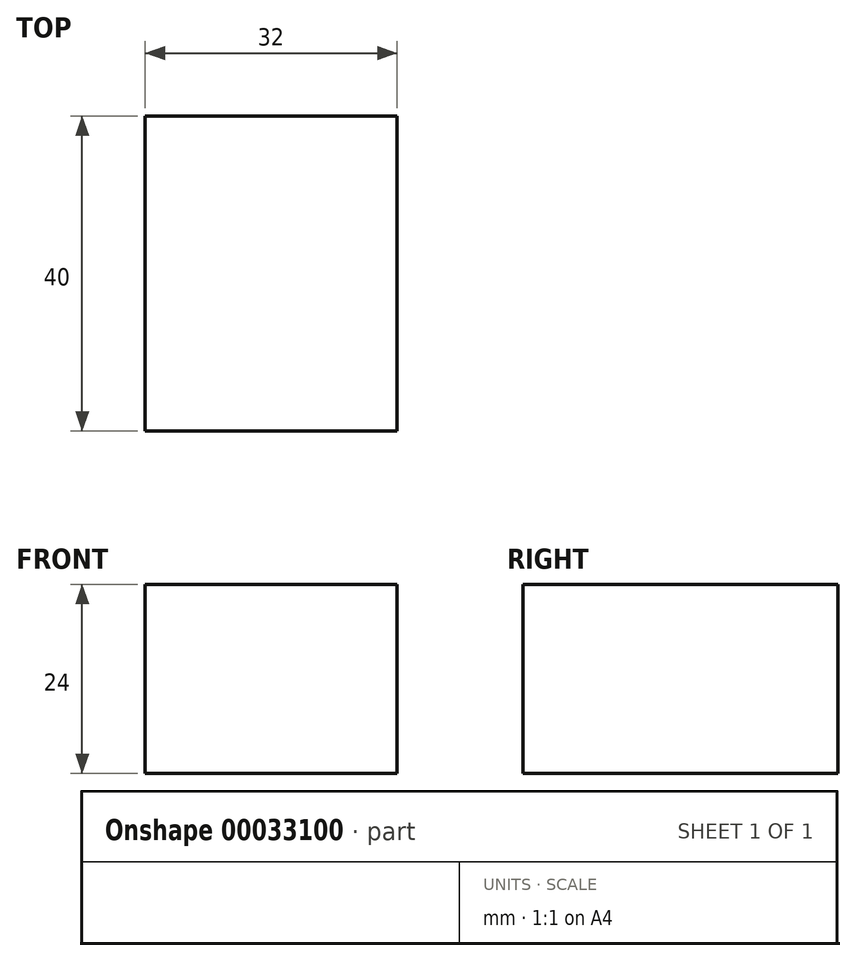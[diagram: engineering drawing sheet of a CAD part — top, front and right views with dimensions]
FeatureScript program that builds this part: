
annotation { "Feature Type Name" : "Feature", "Feature Type Description" : "" }
export const myFeature = defineFeature(function(context is Context, id is Id, definition is map)
    precondition{}
    {
        {
            var Q0;
            Q0=qCreatedBy(makeId("Top.planeOp"),FACE);
            var sketch = newSketch(context, id + "F0", { "sketchPlane" : qUnion([Q0])});
            skLineSegment(sketch, "E0", {"start": v(-49.05, 48.45) * mm, "end": v(-49.05, 8.45) * mm});
            skLineSegment(sketch, "E1", {"start": v(-49.05, 8.45) * mm, "end": v(-17.05, 8.45) * mm});
            skLineSegment(sketch, "E2", {"start": v(-17.05, 8.45) * mm, "end": v(-17.05, 48.45) * mm});
            skLineSegment(sketch, "E3", {"start": v(-17.05, 48.45) * mm, "end": v(-49.05, 48.45) * mm});
            skSolve(sketch);
        }
        {
            var Q0;
            Q0=makeQuery(id+"F0.imprint","IMPRINT",FACE,{"disambiguationData":[TD([[makeQuery(id+"F0.imprint","IMPRINT",EDGE,{"derivedFrom":sQuery(id+"F0.wireOp",EDGE,"E0")}),1.0]])]});
            extrude(context, id + "F1", {"entities" : qUnion([Q0]), "depth" : 24 * mm});
        }
    });
